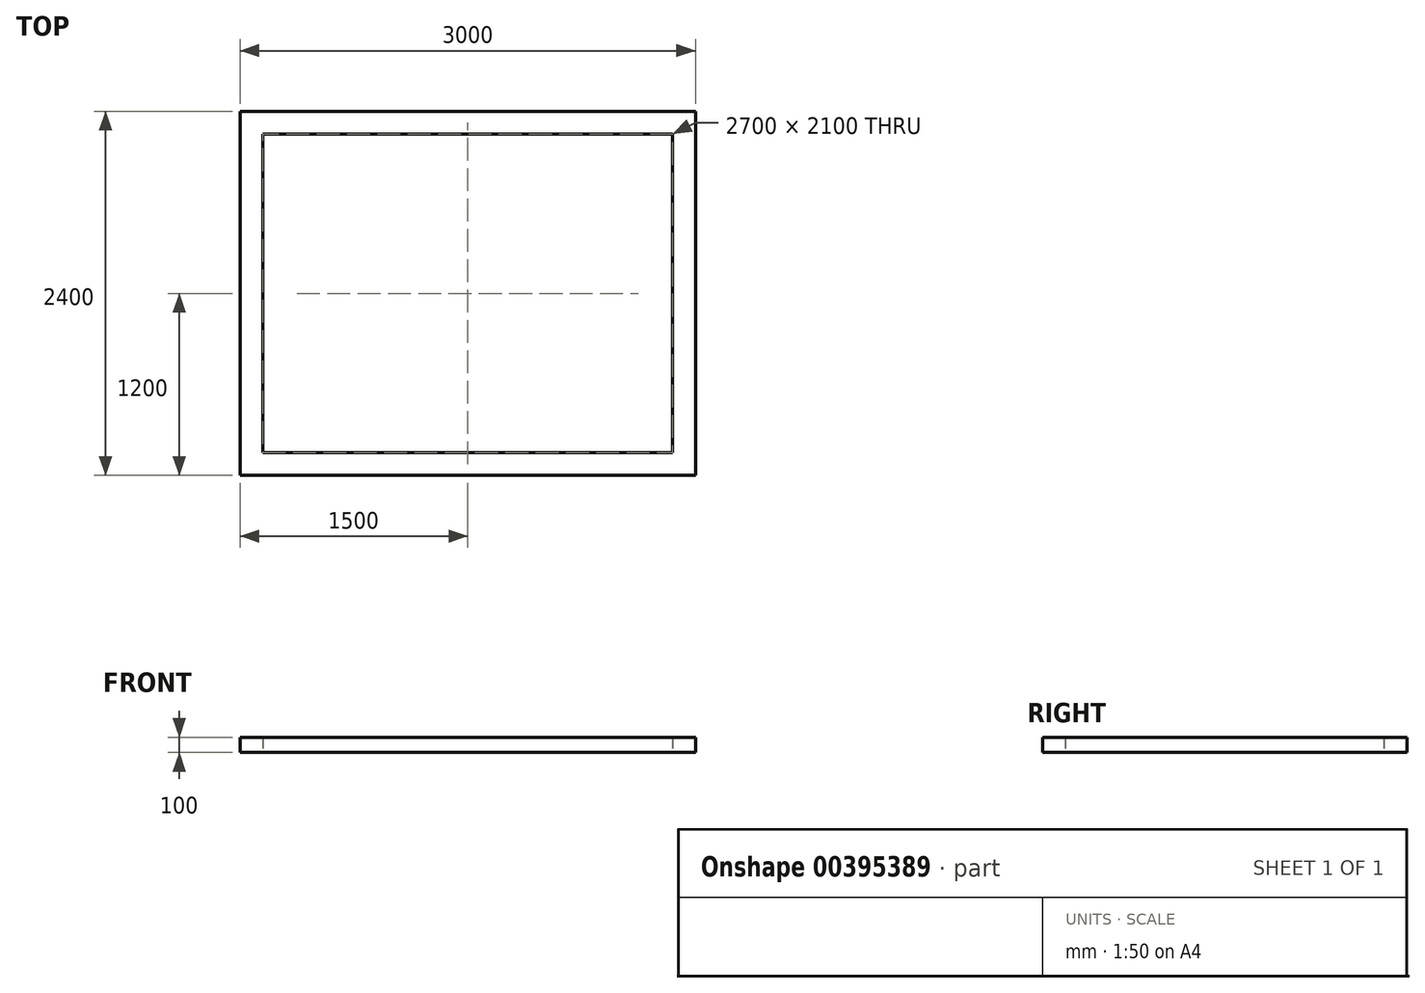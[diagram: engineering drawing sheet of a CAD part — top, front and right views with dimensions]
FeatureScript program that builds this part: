
annotation { "Feature Type Name" : "Feature", "Feature Type Description" : "" }
export const myFeature = defineFeature(function(context is Context, id is Id, definition is map)
    precondition{}
    {
        {
            var Q0;
            Q0=qCreatedBy(makeId("Top.planeOp"),FACE);
            var sketch = newSketch(context, id + "F0", { "sketchPlane" : qUnion([Q0])});
            skLineSegment(sketch, "E0.bottom", {"start": v(0, 1200) * mm, "end": v(1500, 1200) * mm});
            skLineSegment(sketch, "E0.top", {"start": v(0, -1200) * mm, "end": v(1500, -1200) * mm});
            skLineSegment(sketch, "E0.left", {"start": v(0, 1200) * mm, "end": v(0, -1200) * mm, "construction": true});
            skLineSegment(sketch, "E0.right", {"start": v(1500, 1200) * mm, "end": v(1500, -1200) * mm});
            skLineSegment(sketch, "E1", {"start": v(0, 1050) * mm, "end": v(1350, 1050) * mm});
            skLineSegment(sketch, "E2", {"start": v(1350, 1050) * mm, "end": v(1350, -1050) * mm});
            skLineSegment(sketch, "E3", {"start": v(1350, -1050) * mm, "end": v(0, -1050) * mm});
            skLineSegment(sketch, "E4.MirrorCS", {"start": v(-1500, 1200) * mm, "end": v(-1500, -1200) * mm});
            skLineSegment(sketch, "E5.MirrorCS", {"start": v(0, 1050) * mm, "end": v(-1350, 1050) * mm});
            skLineSegment(sketch, "E6.MirrorCS", {"start": v(0, 1200) * mm, "end": v(-1500, 1200) * mm});
            skLineSegment(sketch, "E7.MirrorCS", {"start": v(-1350, 1050) * mm, "end": v(-1350, -1050) * mm});
            skLineSegment(sketch, "E8.MirrorCS", {"start": v(-1350, -1050) * mm, "end": v(0, -1050) * mm});
            skLineSegment(sketch, "E9.MirrorCS", {"start": v(0, -1200) * mm, "end": v(-1500, -1200) * mm});
            skSolve(sketch);
        }
        {
            var Q0;
            Q0=makeQuery(id+"F0.imprint","IMPRINT",FACE,{"disambiguationData":[TD([[makeQuery(id+"F0.imprint","IMPRINT",EDGE,{"derivedFrom":sQuery(id+"F0.wireOp",EDGE,"E0.bottom")}),-1.0]])]});
            extrude(context, id + "F1", {"entities" : qUnion([Q0]), "depth" : 100 * mm});
        }
    });
